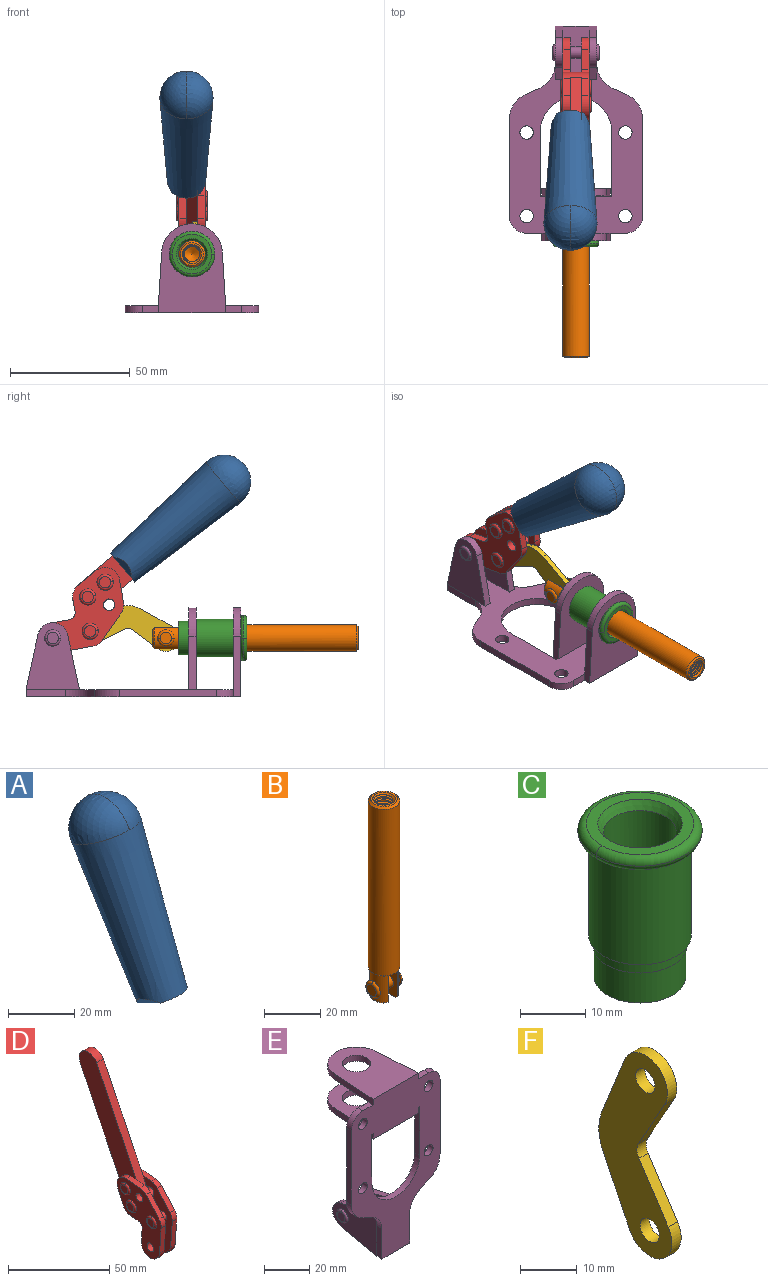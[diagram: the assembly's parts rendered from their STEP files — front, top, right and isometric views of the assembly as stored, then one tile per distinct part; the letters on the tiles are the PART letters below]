
ASSEMBLY  parts=6 mates=6
PART A: 11 faces, bbox 22.3x42.6x64.5 mm
  f0: sphere r=11.13mm, area 411.4mm2, adj f1,f8
  f1: cone r=11.11mm half-angle=3.3deg, axis (0,0.44,0.9), area 3251.8mm2, adj f0,f7,f8,f9,f10
  f2: cylinder r=6.16mm len=11.7mm, axis (1,0,0), area 89.5mm2, adj f3,f4,f5,f6
  f3: plane 60.23x36.75mm, normal (-1,0,0), area 763.6mm2, adj f2,f4,f6,f10
  f4: plane 51.37x25.05mm, normal (0,0.9,-0.44), area 264.2mm2, adj f2,f3,f5,f10
  f5: plane 60.23x36.75mm, normal (1,0,0), area 763.6mm2, adj f2,f4,f6,f10
  f6: plane 51.37x25.05mm, normal (0,-0.9,0.44), area 264.2mm2, adj f2,f3,f5,f10
  f7: plane 9.95x5.95mm, normal (0.71,-0.31,-0.64), area 25.8mm2, adj f1,f10
  f8: sphere r=11.13mm, area 411.4mm2, adj f0,f1
  f9: plane 9.95x5.95mm, normal (-0.71,-0.31,-0.64), area 25.8mm2, adj f1,f10
  f10: plane 14.27x11.38mm, normal (0,-0.44,-0.9), area 106.7mm2, adj f1,f3,f4,f5,f6,f7,f9
PART B: 48 faces, bbox 12.6x11.1x86.1 mm
  f0: torus R=2.41mm, axis (-1,0,0), area 15mm2, adj f30,f32,f34
  f1: torus R=2.41mm, axis (-1,0,0), area 15mm2, adj f29,f31,f33
  f2: cylinder r=5.54mm len=72.39mm, axis (0,0,1), area 2518.5mm2, adj f3,f4,f42,f43
  f3: cone r=5.54mm half-angle=45deg, axis (0,0,1), area 7.6mm2, adj f2,f5,f41
  f4: cone r=5.54mm half-angle=45deg, axis (0,0,-1), area 34.9mm2, adj f2,f39
  f5: cylinder r=5.08mm len=11.48mm, axis (0,0,1), area 108.3mm2, adj f3,f7,f8,f41
  f6: cylinder r=2.41mm len=4.83mm, axis (-1,0,0), area 71.2mm2, adj f40,f41
  f7: cylinder r=2.41mm len=4.83mm, axis (-1,0,0), area 7.6mm2, adj f5,f34
  f8: cone r=5.08mm half-angle=45deg, axis (0,0,1), area 10.6mm2, adj f5,f37,f41
  f9: cone r=3.98mm half-angle=45deg, axis (0,0,1), area 17.6mm2, adj f27,f39,f45,f46,f47
  f10: cylinder r=2.41mm len=4.83mm, axis (-1,0,0), area 7.6mm2, adj f33,f38
  f11: cylinder r=3.2mm len=6.4mm, axis (0,0,1), area 78.4mm2, adj f12,f28,f44,f45,f47
  f12: cylinder r=3.2mm len=6.4mm, axis (0,0,1), area 10.5mm2, adj f11,f13,f45,f47
  f13: cylinder r=3.2mm len=6.4mm, axis (0,0,1), area 10.5mm2, adj f12,f14,f45,f47
  f14: cylinder r=3.2mm len=6.4mm, axis (0,0,1), area 10.5mm2, adj f13,f15,f45,f47
  f15: cylinder r=3.2mm len=6.4mm, axis (0,0,1), area 10.5mm2, adj f14,f16,f45,f47
  f16: cylinder r=3.2mm len=6.4mm, axis (0,0,1), area 10.5mm2, adj f15,f17,f45,f47
  f17: cylinder r=3.2mm len=6.4mm, axis (0,0,1), area 10.5mm2, adj f16,f18,f45,f47
  f18: cylinder r=3.2mm len=6.4mm, axis (0,0,1), area 10.5mm2, adj f17,f19,f45,f47
  f19: cylinder r=3.2mm len=6.4mm, axis (0,0,1), area 10.5mm2, adj f18,f20,f45,f47
  f20: cylinder r=3.2mm len=6.4mm, axis (0,0,1), area 10.5mm2, adj f19,f21,f45,f47
  f21: cylinder r=3.2mm len=6.4mm, axis (0,0,1), area 10.5mm2, adj f20,f22,f45,f47
  f22: cylinder r=3.2mm len=6.4mm, axis (0,0,1), area 10.5mm2, adj f21,f23,f45,f47
  f23: cylinder r=3.2mm len=6.4mm, axis (0,0,1), area 10.5mm2, adj f22,f24,f45,f47
  f24: cylinder r=3.2mm len=6.4mm, axis (0,0,1), area 10.5mm2, adj f23,f25,f45,f47
  f25: cylinder r=3.2mm len=6.4mm, axis (0,0,1), area 10.5mm2, adj f24,f26,f45,f47
  f26: cylinder r=3.2mm len=6.4mm, axis (0,0,1), area 10.5mm2, adj f25,f27,f45,f47
  f27: cylinder r=3.2mm len=6.4mm, axis (0,0,1), area 7.4mm2, adj f9,f26,f45,f47
  f28: cone r=3.2mm half-angle=60deg, axis (0,0,1), area 37.2mm2, adj f11
  f29: plane 4.83x4.83mm, normal (-1,0,0), area 18.3mm2, adj f1,f31
  f30: plane 4.83x4.83mm, normal (1,0,0), area 18.3mm2, adj f0,f32
  f31: torus R=2.41mm, axis (-1,0,0), area 15mm2, adj f1,f29,f33
  f32: torus R=2.41mm, axis (-1,0,0), area 15mm2, adj f0,f30,f34
  f33: plane 6.83x6.83mm, normal (1,0,0), area 18.3mm2, adj f1,f10,f31
  f34: plane 6.83x6.83mm, normal (-1,0,0), area 18.3mm2, adj f0,f7,f32
  f35: cone r=5.08mm half-angle=45deg, axis (0,0,1), area 10.6mm2, adj f36,f38,f40
  f36: plane 7.25x1.97mm, normal (0,0,-1), area 10mm2, adj f35,f40
  f37: plane 7.25x1.97mm, normal (0,0,-1), area 10mm2, adj f8,f41
  f38: cylinder r=5.08mm len=11.48mm, axis (0,0,1), area 108.3mm2, adj f10,f35,f40,f42
  f39: plane 9.55x9.55mm, normal (0,0,1), area 22mm2, adj f4,f9
  f40: plane 12.76x10.09mm, normal (1,0,0), area 95.7mm2, adj f6,f35,f36,f38,f42,f43
  f41: plane 12.76x10.09mm, normal (-1,0,0), area 95.7mm2, adj f3,f5,f6,f8,f37,f43
  f42: cone r=5.54mm half-angle=45deg, axis (0,0,1), area 7.6mm2, adj f2,f38,f40
  f43: plane 11.07x4.7mm, normal (0,0,-1), area 50.4mm2, adj f2,f40,f41
  f44: plane 0.89x0.62mm, normal (-1,0,0), area 0.3mm2, adj f11,f45,f46,f47
  f45: bspline ~24.8x7.63mm, area 266.6mm2, adj f9,f11,f12,f13,f14,f15,f16,f17
  f46: bspline ~24.87x7.63mm, area 73.6mm2, adj f9,f44,f45,f47
  f47: bspline ~24.98x7.63mm, area 272.5mm2, adj f9,f11,f12,f13,f14,f15,f16,f17
PART C: 15 faces, bbox 20.6x20.6x28.7 mm
  f0: torus R=8.26mm, axis (0,0,1), area 56.8mm2, adj f1,f10,f12
  f1: torus R=8.26mm, axis (0,0,1), area 56.8mm2, adj f0,f6,f13
  f2: cylinder r=5.59mm len=25.91mm, axis (0,0,1), area 909.6mm2, adj f3,f4
  f3: cone r=6.86mm half-angle=45deg, axis (0,0,-1), area 70.2mm2, adj f2,f14
  f4: cone r=6.47mm half-angle=30deg, axis (0,0,1), area 66.7mm2, adj f2,f13
  f5: cylinder r=7.04mm len=14.07mm, axis (0,0,1), area 252.6mm2, adj f11,f14
  f6: torus R=8.26mm, axis (0,0,1), area 56.8mm2, adj f1,f12,f13
  f7: cylinder r=7.16mm len=14.33mm, axis (0,0,1), area 91.5mm2, adj f9,f11
  f8: cylinder r=7.86mm len=18.42mm, axis (0,0,1), area 909.6mm2, adj f9,f10
  f9: plane 15.72x15.72mm, normal (0,0,-1), area 33mm2, adj f7,f8
  f10: plane 16.51x16.51mm, normal (0,0,-1), area 19.9mm2, adj f0,f8,f12
  f11: plane 14.33x14.33mm, normal (0,0,-1), area 5.7mm2, adj f5,f7
  f12: torus R=8.26mm, axis (0,0,1), area 56.8mm2, adj f0,f6,f10
  f13: plane 16.51x16.51mm, normal (0,0,1), area 82.7mm2, adj f1,f4,f6
  f14: plane 14.07x14.07mm, normal (0,0,-1), area 7.8mm2, adj f3,f5
PART D: 59 faces, bbox 12.9x60.2x99.6 mm
  f0: torus R=2.39mm, axis (-1,0,0), area 14.9mm2, adj f20,f43,f51
  f1: torus R=2.39mm, axis (-1,0,0), area 14.9mm2, adj f19,f42,f51
  f2: torus R=2.39mm, axis (-1,0,0), area 14.9mm2, adj f18,f35,f51
  f3: torus R=2.39mm, axis (-1,0,0), area 14.9mm2, adj f14,f17,f23
  f4: torus R=2.39mm, axis (-1,0,0), area 14.9mm2, adj f13,f16,f23
  f5: torus R=2.39mm, axis (-1,0,0), area 14.9mm2, adj f12,f15,f23
  f6: cylinder r=2.39mm len=4.78mm, axis (1,0,0), area 46.5mm2, adj f48,f50,f51
  f7: cylinder r=2.39mm len=4.78mm, axis (1,0,0), area 46.5mm2, adj f50,f51
  f8: cylinder r=6.35mm len=12.68mm, axis (1,0,0), area 61.8mm2, adj f38,f39,f50,f51
  f9: cylinder r=2.39mm len=4.78mm, axis (-1,0,0), area 70.5mm2, adj f46,f50
  f10: cylinder r=2.39mm len=4.78mm, axis (-1,0,0), area 46.5mm2, adj f23,f45,f46
  f11: cylinder r=2.39mm len=4.78mm, axis (-1,0,0), area 46.5mm2, adj f23,f46
  f12: plane 4.78x4.78mm, normal (1,0,0), area 17.9mm2, adj f5,f15
  f13: plane 4.78x4.78mm, normal (1,0,0), area 17.9mm2, adj f4,f16
  f14: plane 4.78x4.78mm, normal (1,0,0), area 17.9mm2, adj f3,f17
  f15: torus R=2.39mm, axis (-1,0,0), area 14.9mm2, adj f5,f12,f23
  f16: torus R=2.39mm, axis (-1,0,0), area 14.9mm2, adj f4,f13,f23
  f17: torus R=2.39mm, axis (-1,0,0), area 14.9mm2, adj f3,f14,f23
  f18: plane 4.78x4.78mm, normal (-1,0,0), area 17.9mm2, adj f2,f35
  f19: plane 4.78x4.78mm, normal (-1,0,0), area 17.9mm2, adj f1,f42
  f20: plane 4.78x4.78mm, normal (-1,0,0), area 17.9mm2, adj f0,f43
  f21: plane 2.26x0.2mm, normal (1,0,0), area 0.2mm2, adj f31,f44
  f22: plane 2.26x0.2mm, normal (-1,0,0), area 0.2mm2, adj f41,f44
  f23: plane 39.37x30.77mm, normal (1,0,0), area 565.5mm2, adj f3,f4,f5,f10,f11,f15,f16,f17
  f24: cylinder r=6.1mm len=4.15mm, axis (-1,0,0), area 14.7mm2, adj f23,f25,f32,f46
  f25: plane 10.25x9.01mm, normal (0,-0.75,0.66), area 42.3mm2, adj f23,f24,f26,f46
  f26: cylinder r=6.35mm len=4.64mm, axis (-1,0,0), area 15.6mm2, adj f23,f25,f27,f46
  f27: plane 15.84x3.1mm, normal (0,-1,-0.07), area 49.2mm2, adj f23,f26,f28,f46
  f28: cylinder r=6.35mm len=12.68mm, axis (-1,0,0), area 61.8mm2, adj f23,f27,f29,f46
  f29: plane 8.11x3.1mm, normal (0,1,0.07), area 25.2mm2, adj f23,f28,f30,f46
  f30: cylinder r=3.05mm len=3.25mm, axis (-1,0,0), area 14.8mm2, adj f23,f29,f31,f46
  f31: plane 5.99x3.1mm, normal (0,0.07,-1), area 18.6mm2, adj f21,f23,f30,f44,f46
  f32: plane 9.5x3.1mm, normal (0,-0.07,1), area 29.5mm2, adj f23,f24,f33,f46,f47
  f33: cylinder r=6.1mm len=8.63mm, axis (-1,0,0), area 39.1mm2, adj f23,f32,f34,f47
  f34: plane 8.65x3.96mm, normal (0,0.91,-0.42), area 29.5mm2, adj f23,f33,f44,f47
  f35: torus R=2.39mm, axis (-1,0,0), area 14.9mm2, adj f2,f18,f51
  f36: plane 10.25x9.01mm, normal (0,-0.75,0.66), area 42.3mm2, adj f37,f49,f50,f51
  f37: cylinder r=6.35mm len=4.64mm, axis (1,0,0), area 15.6mm2, adj f36,f38,f50,f51
  f38: plane 15.84x3.1mm, normal (0,-1,-0.07), area 49.2mm2, adj f8,f37,f50,f51
  f39: plane 8.11x3.1mm, normal (0,1,0.07), area 25.2mm2, adj f8,f40,f50,f51
  f40: cylinder r=3.05mm len=3.25mm, axis (1,0,0), area 14.8mm2, adj f39,f41,f50,f51
  f41: plane 5.99x3.1mm, normal (0,0.07,-1), area 18.6mm2, adj f22,f40,f44,f50,f51
  f42: torus R=2.39mm, axis (-1,0,0), area 14.9mm2, adj f1,f19,f51
  f43: torus R=2.39mm, axis (-1,0,0), area 14.9mm2, adj f0,f20,f51
  f44: cylinder r=6.35mm len=12.12mm, axis (-1,0,0), area 128.9mm2, adj f21,f22,f23,f31,f34,f41,f46,f47
  f45: plane 2.65x1.35mm, normal (1,0,0), area 1mm2, adj f10,f55
  f46: plane 39.08x20.42mm, normal (-1,0,0), area 412.5mm2, adj f9,f10,f11,f24,f25,f26,f27,f28
  f47: plane 77.62x39.82mm, normal (1,0,0), area 850mm2, adj f32,f33,f34,f44,f53,f54,f55
  f48: plane 2.65x1.35mm, normal (-1,0,0), area 1mm2, adj f6,f55
  f49: cylinder r=6.1mm len=4.15mm, axis (1,0,0), area 14.7mm2, adj f36,f50,f51,f56
  f50: plane 39.08x20.42mm, normal (1,0,0), area 412.5mm2, adj f6,f7,f8,f9,f36,f37,f38,f39
  f51: plane 39.37x30.77mm, normal (-1,0,0), area 565.5mm2, adj f0,f1,f2,f6,f7,f8,f35,f36
  f52: plane 8.65x3.96mm, normal (0,0.91,-0.42), area 29.5mm2, adj f44,f51,f57,f58
  f53: plane 68.49x33.4mm, normal (0,0.9,-0.44), area 358.1mm2, adj f44,f47,f54,f58
  f54: cylinder r=6.35mm len=12.06mm, axis (1,0,0), area 93.7mm2, adj f47,f53,f55,f58
  f55: plane 68.49x33.4mm, normal (0,-0.9,0.44), area 358.1mm2, adj f44,f45,f46,f47,f48,f50,f54,f58
  f56: plane 9.5x3.1mm, normal (0,-0.07,1), area 29.5mm2, adj f49,f50,f51,f57,f58
  f57: cylinder r=6.1mm len=8.63mm, axis (1,0,0), area 39.1mm2, adj f51,f52,f56,f58
  f58: plane 77.62x39.82mm, normal (-1,0,0), area 850mm2, adj f44,f52,f53,f54,f55,f56,f57
PART E: 55 faces, bbox 55.7x37.4x89.8 mm
  f0: torus R=2.41mm, axis (-1,0,0), area 15mm2, adj f11,f15,f25
  f1: torus R=2.41mm, axis (-1,0,0), area 15mm2, adj f10,f12,f22
  f2: cylinder r=2.78mm len=5.56mm, axis (0,-1,0), area 54.2mm2, adj f30,f54
  f3: cylinder r=14.99mm len=29.97mm, axis (0,-1,0), area 145.9mm2, adj f30,f49,f53,f54
  f4: cylinder r=2.78mm len=5.56mm, axis (0,-1,0), area 54.2mm2, adj f30,f54
  f5: cylinder r=2.78mm len=5.56mm, axis (0,-1,0), area 54.2mm2, adj f30,f54
  f6: cylinder r=2.78mm len=5.56mm, axis (0,-1,0), area 54.2mm2, adj f30,f54
  f7: cylinder r=6.35mm len=12.7mm, axis (0,0,1), area 123.6mm2, adj f27,f51
  f8: cylinder r=6.35mm len=12.7mm, axis (0,0,-1), area 124.7mm2, adj f21,f35
  f9: cylinder r=2.41mm len=11.18mm, axis (-1,0,0), area 169.4mm2, adj f16,f19
  f10: plane 4.83x4.83mm, normal (1,0,0), area 18.3mm2, adj f1,f12
  f11: plane 4.83x4.83mm, normal (-1,0,0), area 18.3mm2, adj f0,f15
  f12: torus R=2.41mm, axis (-1,0,0), area 15mm2, adj f1,f10,f22
  f13: cylinder r=6.35mm len=12.41mm, axis (1,0,0), area 53.4mm2, adj f18,f19,f22,f23
  f14: cylinder r=6.35mm len=12.41mm, axis (-1,0,0), area 53.4mm2, adj f16,f17,f24,f25
  f15: torus R=2.41mm, axis (-1,0,0), area 15mm2, adj f0,f11,f25
  f16: plane 27.86x22.35mm, normal (1,0,0), area 425.4mm2, adj f9,f14,f17,f24,f30
  f17: plane 22.86x4.97mm, normal (0,0.21,0.98), area 72.5mm2, adj f14,f16,f25,f30
  f18: plane 22.86x4.97mm, normal (0,0.21,0.98), area 72.5mm2, adj f13,f19,f22,f30
  f19: plane 27.86x22.35mm, normal (-1,0,0), area 425.4mm2, adj f9,f13,f18,f23,f30
  f20: cylinder r=12.7mm len=25.35mm, axis (0,0,-1), area 119.8mm2, adj f21,f34,f35,f36
  f21: plane 34.21x28.07mm, normal (0,0,-1), area 702.4mm2, adj f8,f20,f30,f34,f36
  f22: plane 27.96x22.45mm, normal (1,0,0), area 407.2mm2, adj f1,f12,f13,f18,f23,f30,f42,f43
  f23: plane 22.86x4.97mm, normal (0,0.21,-0.98), area 72.5mm2, adj f13,f19,f22,f44
  f24: plane 22.86x4.97mm, normal (0,0.21,-0.98), area 72.5mm2, adj f14,f16,f25,f44
  f25: plane 27.86x22.35mm, normal (-1,0,0), area 407.1mm2, adj f0,f14,f15,f17,f24,f30,f45,f46
  f26: plane 3.1x0.95mm, normal (0,0,-1), area 2.7mm2, adj f30,f49,f50,f54
  f27: plane 34.21x28.07mm, normal (0,0,1), area 702.4mm2, adj f7,f28,f30,f50,f52
  f28: cylinder r=12.7mm len=25.35mm, axis (0,0,1), area 118.8mm2, adj f27,f50,f51,f52
  f29: plane 3.1x0.95mm, normal (0,0,-1), area 2.7mm2, adj f30,f52,f53,f54
  f30: plane 86.54x55.63mm, normal (0,1,0), area 2362.9mm2, adj f2,f3,f4,f5,f6,f16,f17,f18
  f31: plane 40.56x3.1mm, normal (-1,0,0), area 125.7mm2, adj f30,f32,f48,f54
  f32: cylinder r=7.11mm len=7.11mm, axis (0,-1,0), area 34.6mm2, adj f30,f31,f33,f54
  f33: plane 6.67x3.1mm, normal (0,0,1), area 20.4mm2, adj f30,f32,f34,f54
  f34: plane 25.39x3.13mm, normal (-1,0.06,0), area 79.5mm2, adj f20,f21,f33,f35,f54
  f35: plane 37.31x28.45mm, normal (0,0,1), area 789.9mm2, adj f8,f20,f34,f36,f54
  f36: plane 25.39x3.13mm, normal (1,0.06,0), area 79.5mm2, adj f20,f21,f35,f37,f54
  f37: plane 6.67x3.1mm, normal (0,0,1), area 20.4mm2, adj f30,f36,f38,f54
  f38: cylinder r=7.11mm len=7.11mm, axis (0,-1,0), area 34.6mm2, adj f30,f37,f39,f54
  f39: plane 40.56x3.1mm, normal (1,0,0), area 125.7mm2, adj f30,f38,f40,f54
  f40: cylinder r=11.18mm len=10.16mm, axis (0,-1,0), area 39.5mm2, adj f30,f39,f41,f54
  f41: plane 6.09x3.1mm, normal (0.42,0,-0.91), area 20.8mm2, adj f30,f40,f42,f54
  f42: cylinder r=11.18mm len=9.41mm, axis (0,-1,0), area 37.2mm2, adj f22,f30,f41,f43,f54
  f43: plane 16.5x3.1mm, normal (1,0,0), area 51.1mm2, adj f22,f42,f44,f54
  f44: plane 17.37x3.1mm, normal (0,0,-1), area 53.8mm2, adj f23,f24,f30,f43,f45,f54
  f45: plane 16.5x3.1mm, normal (-1,0,0), area 51.1mm2, adj f25,f44,f46,f54
  f46: cylinder r=11.18mm len=9.41mm, axis (0,-1,0), area 37.2mm2, adj f25,f30,f45,f47,f54
  f47: plane 6.09x3.1mm, normal (-0.42,0,-0.91), area 20.8mm2, adj f30,f46,f48,f54
  f48: cylinder r=11.18mm len=10.16mm, axis (0,-1,0), area 39.5mm2, adj f30,f31,f47,f54
  f49: plane 26.54x3.1mm, normal (-1,0,0), area 82.3mm2, adj f3,f26,f30,f54
  f50: plane 25.39x3.1mm, normal (1,0.06,0), area 78.8mm2, adj f26,f27,f28,f51,f54
  f51: plane 37.31x28.45mm, normal (0,0,-1), area 789.9mm2, adj f7,f28,f50,f52,f54
  f52: plane 25.39x3.1mm, normal (-1,0.06,0), area 78.8mm2, adj f27,f28,f29,f51,f54
  f53: plane 26.54x3.1mm, normal (1,0,0), area 82.3mm2, adj f3,f29,f30,f54
  f54: plane 89.66x55.63mm, normal (0,-1,0), area 2678.5mm2, adj f2,f3,f4,f5,f6,f26,f29,f31
PART F: 12 faces, bbox 2.3x18.2x42.8 mm
  f0: cylinder r=2.4mm len=4.8mm, axis (1,0,0), area 34.9mm2, adj f4,f11
  f1: cylinder r=10.41mm len=8.47mm, axis (1,0,0), area 20.2mm2, adj f4,f9,f10,f11
  f2: cylinder r=3.05mm len=3.16mm, axis (1,0,0), area 7.7mm2, adj f4,f6,f7,f11
  f3: cylinder r=2.4mm len=4.8mm, axis (1,0,0), area 34.9mm2, adj f4,f11
  f4: plane 42.81x18.23mm, normal (-1,0,0), area 414.1mm2, adj f0,f1,f2,f3,f5,f6,f7,f8
  f5: cylinder r=5.54mm len=10.67mm, axis (1,0,0), area 41.8mm2, adj f4,f6,f10,f11
  f6: plane 11.66x6.53mm, normal (0,-0.87,-0.49), area 30.9mm2, adj f2,f4,f5,f11
  f7: plane 11.17x7.33mm, normal (0,-0.84,0.55), area 30.9mm2, adj f2,f4,f8,f11
  f8: cylinder r=5.54mm len=10.51mm, axis (1,0,0), area 41.8mm2, adj f4,f7,f9,f11
  f9: plane 13.67x6.67mm, normal (0,0.9,-0.44), area 35.1mm2, adj f1,f4,f8,f11
  f10: plane 14.1x5.7mm, normal (0,0.93,0.37), area 35.1mm2, adj f1,f4,f5,f11
  f11: plane 42.81x18.23mm, normal (1,0,0), area 414.1mm2, adj f0,f1,f2,f3,f5,f6,f7,f8
PLACE A rot(axis=(1,0,0),75.8deg) t=(-2.31,4.07,17.79)mm
PLACE B rot(axis=(1,0,0),90deg) t=(0,9.46,9.14)mm
PLACE C rot(axis=(1,0,0),90deg) t=(0,9.14,9.14)mm
PLACE D rot(axis=(1,0,0),75.8deg) t=(0,4.07,17.79)mm
PLACE E rot(axis=(1,0,0),90deg) t=(0,9.14,9.14)mm fixed
PLACE F rot(axis=(0,-0.69,-0.73),180deg) t=(1.16,11.49,11.16)mm
MATE fastened A.f2 <-> D.f54  axis (1,0,0) through (0,-31.54,100.13)mm
MATE revolute D.f7 <-> E.f0  axis (-1,0,0) through (0,41.23,33.75)mm
MATE slider B.f2 <-> C.f2  axis (0,-1,0) through (0,-49.32,33.75)mm
MATE revolute D.f4 <-> F.f5  axis (-1,0,0) through (0,25.61,36.58)mm
MATE fastened C.f0 <-> E.f7  axis (0,1,0) through (0,-37.25,33.75)mm
MATE revolute F.f3 <-> B.f6  axis (-1,0,0) through (0,-6.01,33.75)mm
